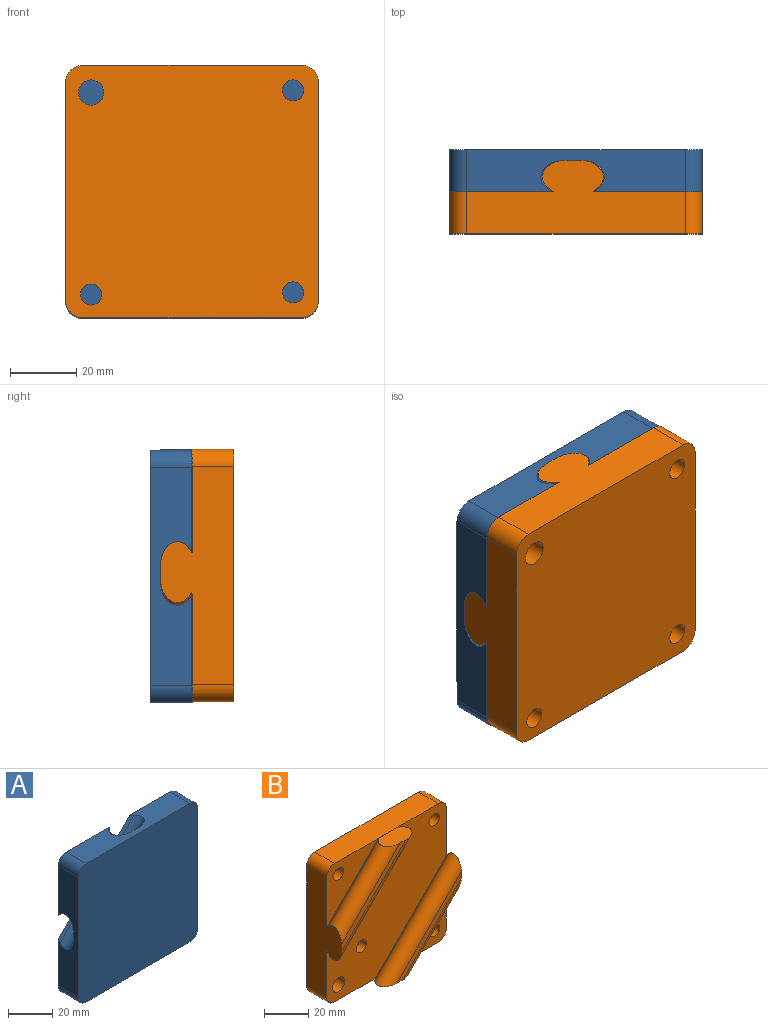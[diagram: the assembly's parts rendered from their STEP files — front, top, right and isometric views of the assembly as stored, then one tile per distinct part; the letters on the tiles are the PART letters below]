
ASSEMBLY  parts=2 mates=1
PART A: 243 faces, bbox 83.4x12.7x83.4 mm
  f0: plane 54.93x54.62mm, normal (0,1,0), area 1341.8mm2, adj f27,f28,f29,f30,f37,f38,f39,f40
  f1: plane 76.2x76.2mm, normal (0,1,0), area 2254mm2, adj f2,f3,f5,f7,f8,f9,f10,f19
  f2: plane 66.04x12.7mm, normal (0,0,-1), area 680.5mm2, adj f1,f4,f5,f14,f15,f18,f20,f22
  f3: plane 66.04x12.7mm, normal (1,0,0), area 680.5mm2, adj f1,f4,f5,f14,f15,f18,f19,f22
  f4: plane 41.48x41.48mm, normal (0,1,0), area 187.6mm2, adj f2,f3,f23,f24
  f5: plane 46.98x46.98mm, normal (0.54,-0.64,-0.54), area 102.9mm2, adj f1,f2,f3,f24
  f6: plane 41.48x41.48mm, normal (0,1,0), area 187.6mm2, adj f7,f8,f25,f26
  f7: plane 66.04x12.7mm, normal (0,0,1), area 680.5mm2, adj f1,f6,f9,f12,f13,f19,f21,f22
  f8: plane 66.04x12.7mm, normal (-1,0,0), area 680.5mm2, adj f1,f6,f9,f12,f13,f20,f21,f22
  f9: plane 46.98x46.98mm, normal (-0.54,-0.64,0.54), area 102.9mm2, adj f1,f7,f8,f26
  f10: cylinder r=3.3mm len=7.59mm, axis (0,1,0), area 157.6mm2, adj f1,f11
  f11: plane 6.6x6.6mm, normal (0,1,0), area 27mm2, adj f10,f16
  f12: plane 32.6x32.6mm, normal (0.54,-0.64,-0.54), area 70.9mm2, adj f7,f8,f13,f25
  f13: plane 32.6x32.6mm, normal (0,1,0), area 525.9mm2, adj f7,f8,f12,f21
  f14: plane 32.6x32.6mm, normal (-0.54,-0.64,0.54), area 70.9mm2, adj f2,f3,f15,f23
  f15: plane 32.6x32.6mm, normal (0,1,0), area 525.9mm2, adj f2,f3,f14,f18
  f16: cylinder r=1.52mm len=3.05mm, axis (0,1,0), area 9.3mm2, adj f11,f17
  f17: plane 3.05x3.05mm, normal (0,1,0), area 7.3mm2, adj f16
  f18: cylinder r=5.08mm len=12.7mm, axis (0,-1,0), area 101.3mm2, adj f2,f3,f15,f22
  f19: cylinder r=5.08mm len=12.7mm, axis (0,1,0), area 101.3mm2, adj f1,f3,f7,f22
  f20: cylinder r=5.08mm len=12.7mm, axis (0,1,0), area 101.3mm2, adj f1,f2,f8,f22
  f21: cylinder r=5.08mm len=12.7mm, axis (0,-1,0), area 101.3mm2, adj f7,f8,f13,f22
  f22: plane 76.2x76.2mm, normal (0,-1,0), area 5784.3mm2, adj f2,f3,f7,f8,f18,f19,f20,f21
  f23: cylinder r=5.08mm len=40.27mm, axis (-0.71,0,-0.71), area 513.1mm2, adj f2,f3,f4,f14
  f24: cylinder r=5.08mm len=52.26mm, axis (0.71,0,0.71), area 760.9mm2, adj f2,f3,f4,f5
  f25: cylinder r=5.08mm len=40.27mm, axis (-0.71,0,-0.71), area 513.1mm2, adj f6,f7,f8,f12
  f26: cylinder r=5.08mm len=52.26mm, axis (-0.71,0,-0.71), area 760.9mm2, adj f6,f7,f8,f9
  f27: plane 21.83x21.27mm, normal (-0.72,0,-0.7), area 271mm2, adj f0,f1,f28,f30
  f28: plane 33.66x32.79mm, normal (-0.7,0,0.72), area 417.7mm2, adj f0,f1,f27,f29
  f29: plane 21.83x21.27mm, normal (0.72,0,0.7), area 271mm2, adj f0,f1,f28,f30
  f30: plane 33.66x32.79mm, normal (0.7,0,-0.72), area 417.7mm2, adj f0,f1,f27,f29
  f31: plane 2.54x0.4mm, normal (-0.7,0,0.71), area 1.4mm2, adj f32,f45,f46,f47
  f32: plane 2.54x1.56mm, normal (-0.71,0,-0.7), area 5.6mm2, adj f31,f33,f46,f47
  f33: plane 2.54x0.5mm, normal (0.7,0,-0.71), area 1.8mm2, adj f32,f34,f46,f47
  f34: extruded ~2.54x0.95mm, area 2.9mm2, adj f33,f35,f46,f47
  f35: extruded ~2.54x0.81mm, area 2.3mm2, adj f34,f36,f46,f47
  f36: extruded ~2.54x0.87mm, area 2.5mm2, adj f35,f45,f46,f47
  f37: extruded ~2.54x1.33mm, area 3.8mm2, adj f0,f38,f44,f46
  f38: extruded ~2.62x2.54mm, area 7.7mm2, adj f0,f37,f39,f46
  f39: plane 2.54x1.04mm, normal (-0.7,0,0.71), area 3.7mm2, adj f0,f38,f40,f46
  f40: plane 3.94x3.91mm, normal (0.71,0,0.7), area 14.1mm2, adj f0,f39,f41,f46
  f41: plane 2.54x0.5mm, normal (0.7,0,-0.71), area 1.8mm2, adj f0,f40,f42,f46
  f42: plane 2.54x1.53mm, normal (-0.71,0,-0.7), area 5.5mm2, adj f0,f41,f43,f46
  f43: plane 2.54x0.45mm, normal (0.7,0,-0.71), area 1.6mm2, adj f0,f42,f44,f46
  f44: extruded ~2.54x1.48mm, area 4.4mm2, adj f0,f37,f43,f46
  f45: extruded ~2.54x1.04mm, area 3.2mm2, adj f31,f36,f46,f47
  f46: plane 6.02x4.43mm, normal (0,1,0), area 8.1mm2, adj f31,f32,f33,f34,f35,f36,f37,f38
  f47: plane 2.67x2.65mm, normal (0,1,0), area 4.1mm2, adj f31,f32,f33,f34,f35,f36,f45
  f48: extruded ~2.54x0.86mm, area 2.5mm2, adj f49,f75,f76,f77
  f49: extruded ~2.54x0.52mm, area 1.5mm2, adj f48,f50,f76,f77
  f50: extruded ~2.54x0.5mm, area 1.4mm2, adj f49,f51,f76,f77
  f51: extruded ~2.54x0.68mm, area 1.9mm2, adj f50,f52,f76,f77
  f52: extruded ~2.54x0.9mm, area 2.7mm2, adj f51,f53,f76,f77
  f53: plane 2.54x0.46mm, normal (0.67,0,-0.74), area 1.6mm2, adj f52,f54,f76,f77
  f54: plane 2.54x0.27mm, normal (0.71,0,0.7), area 1mm2, adj f53,f75,f76,f77
  f55: plane 2.54x0.51mm, normal (0.85,0,0.53), area 1.5mm2, adj f0,f56,f74,f76
  f56: plane 2.54x0.35mm, normal (0.7,0,-0.71), area 1.3mm2, adj f0,f55,f57,f76
  f57: plane 2.54x2.01mm, normal (-0.71,0,-0.7), area 7.2mm2, adj f0,f56,f58,f76
  f58: extruded ~2.54x1.01mm, area 2.9mm2, adj f0,f57,f59,f76
  f59: extruded ~2.54x1.03mm, area 3mm2, adj f0,f58,f60,f76
  f60: extruded ~2.54x0.59mm, area 1.9mm2, adj f0,f59,f61,f76
  f61: extruded ~2.54x0.67mm, area 1.9mm2, adj f0,f60,f62,f76
  f62: plane 2.54x0.51mm, normal (0.92,0,0.38), area 1.4mm2, adj f0,f61,f63,f76
  f63: extruded ~2.54x0.55mm, area 1.5mm2, adj f0,f62,f64,f76
  f64: extruded ~2.54x0.51mm, area 1.6mm2, adj f0,f63,f65,f76
  f65: extruded ~2.54x0.62mm, area 1.8mm2, adj f0,f64,f66,f76
  f66: extruded ~2.54x0.64mm, area 1.9mm2, adj f0,f65,f67,f76
  f67: plane 2.54x0.18mm, normal (0.71,0,0.7), area 0.6mm2, adj f0,f66,f68,f76
  f68: plane 2.54x0.52mm, normal (-0.68,0,0.74), area 1.8mm2, adj f0,f67,f69,f76
  f69: extruded ~2.54x2.35mm, area 6.9mm2, adj f0,f68,f70,f76
  f70: extruded ~2.54x0.89mm, area 2.6mm2, adj f0,f69,f71,f76
  f71: extruded ~2.54x0.91mm, area 2.6mm2, adj f0,f70,f72,f76
  f72: extruded ~2.54x0.65mm, area 2mm2, adj f0,f71,f73,f76
  f73: extruded ~2.54x0.81mm, area 2.1mm2, adj f0,f72,f74,f76
  f74: plane 2.54x0.02mm, normal (0.7,0,-0.71), area 0.1mm2, adj f0,f55,f73,f76
  f75: extruded ~2.54x0.85mm, area 2.5mm2, adj f48,f54,f76,f77
  f76: plane 4.8x4.5mm, normal (0,1,0), area 7.2mm2, adj f48,f49,f50,f51,f52,f53,f54,f55
  f77: plane 2.27x1.72mm, normal (0,1,0), area 2.5mm2, adj f48,f49,f50,f51,f52,f53,f54,f75
  f78: plane 2.54x1.9mm, normal (-0.71,0,-0.7), area 6.8mm2, adj f0,f79,f94,f95
  f79: plane 2.54x0.49mm, normal (-0.7,0,0.71), area 1.8mm2, adj f0,f78,f80,f95
  f80: plane 2.54x1.94mm, normal (0.71,0,0.7), area 6.9mm2, adj f0,f79,f81,f95
  f81: extruded ~2.54x1.09mm, area 3.2mm2, adj f0,f80,f82,f95
  f82: extruded ~2.54x1.05mm, area 3.1mm2, adj f0,f81,f83,f95
  f83: extruded ~2.54x0.68mm, area 2.1mm2, adj f0,f82,f84,f95
  f84: extruded ~2.54x0.7mm, area 1.8mm2, adj f0,f83,f85,f95
  f85: plane 2.54x0.02mm, normal (0.7,0,-0.71), area 0.1mm2, adj f0,f84,f86,f95
  f86: plane 2.54x0.46mm, normal (0.82,0,0.57), area 1.4mm2, adj f0,f85,f87,f95
  f87: plane 2.54x0.4mm, normal (0.7,0,-0.71), area 1.4mm2, adj f0,f86,f88,f95
  f88: plane 2.96x2.93mm, normal (-0.71,0,-0.7), area 10.6mm2, adj f0,f87,f89,f95
  f89: plane 2.54x0.49mm, normal (-0.7,0,0.71), area 1.7mm2, adj f0,f88,f90,f95
  f90: plane 2.54x1.54mm, normal (0.71,0,0.7), area 5.5mm2, adj f0,f89,f91,f95
  f91: extruded ~2.54x1.02mm, area 3.1mm2, adj f0,f90,f92,f95
  f92: extruded ~2.54x0.91mm, area 2.6mm2, adj f0,f91,f93,f95
  f93: extruded ~2.54x0.67mm, area 1.9mm2, adj f0,f92,f94,f95
  f94: extruded ~2.54x0.69mm, area 2mm2, adj f0,f78,f93,f95
  f95: plane 5.44x4.98mm, normal (0,1,0), area 6.8mm2, adj f78,f79,f80,f81,f82,f83,f84,f85
  f96: plane 2.54x0.48mm, normal (0.7,0,-0.71), area 1.7mm2, adj f0,f97,f99,f100
  f97: plane 4.19x4.16mm, normal (-0.71,0,-0.7), area 15mm2, adj f0,f96,f98,f100
  f98: plane 2.54x0.48mm, normal (-0.7,0,0.71), area 1.7mm2, adj f0,f97,f99,f100
  f99: plane 4.19x4.16mm, normal (0.71,0,0.7), area 15mm2, adj f0,f96,f98,f100
  f100: plane 4.67x4.64mm, normal (0,1,0), area 4mm2, adj f96,f97,f98,f99
  f101: plane 3.94x3.91mm, normal (0.71,0,0.7), area 14.1mm2, adj f0,f102,f106,f107
  f102: plane 2.54x2.22mm, normal (0.7,0,-0.71), area 7.9mm2, adj f0,f101,f103,f107
  f103: plane 2.54x0.44mm, normal (-0.71,0,-0.7), area 1.6mm2, adj f0,f102,f104,f107
  f104: plane 2.54x1.72mm, normal (-0.7,0,0.71), area 6.2mm2, adj f0,f103,f105,f107
  f105: plane 3.49x3.47mm, normal (-0.71,0,-0.7), area 12.5mm2, adj f0,f104,f106,f107
  f106: plane 2.54x0.5mm, normal (-0.7,0,0.71), area 1.8mm2, adj f0,f101,f105,f107
  f107: plane 6.13x4.4mm, normal (0,1,0), area 5.4mm2, adj f101,f102,f103,f104,f105,f106
  f108: extruded ~2.54x1.06mm, area 3.2mm2, adj f109,f123,f124,f125
  f109: extruded ~2.54x1.97mm, area 5.8mm2, adj f108,f110,f124,f125
  f110: extruded ~2.54x0.93mm, area 2.6mm2, adj f109,f111,f124,f125
  f111: extruded ~2.54x1.06mm, area 3.2mm2, adj f110,f112,f124,f125
  f112: extruded ~2.54x1.06mm, area 3.2mm2, adj f111,f113,f124,f125
  f113: extruded ~2.54x0.93mm, area 2.6mm2, adj f112,f123,f124,f125
  f114: extruded ~2.54x1.49mm, area 4.4mm2, adj f0,f115,f122,f124
  f115: extruded ~2.54x1.48mm, area 4.3mm2, adj f0,f114,f116,f124
  f116: extruded ~2.54x1.4mm, area 4mm2, adj f0,f115,f117,f124
  f117: extruded ~2.54x1.41mm, area 4mm2, adj f0,f116,f118,f124
  f118: extruded ~2.54x1.48mm, area 4.3mm2, adj f0,f117,f119,f124
  f119: extruded ~2.54x0.98mm, area 3mm2, adj f0,f118,f120,f124
  f120: extruded ~2.54x1.01mm, area 2.6mm2, adj f0,f119,f121,f124
  f121: extruded ~2.54x0.89mm, area 2.7mm2, adj f0,f120,f122,f124
  f122: extruded ~2.54x1.42mm, area 4mm2, adj f0,f114,f121,f124
  f123: extruded ~2.54x0.93mm, area 2.6mm2, adj f108,f113,f124,f125
  f124: plane 4.33x4.28mm, normal (0,1,0), area 7.1mm2, adj f108,f109,f110,f111,f112,f113,f114,f115
  f125: plane 3.21x3.06mm, normal (0,1,0), area 6.4mm2, adj f108,f109,f110,f111,f112,f113,f123
  f126: extruded ~2.54x1.38mm, area 3.9mm2, adj f0,f127,f140,f141
  f127: extruded ~2.54x0.92mm, area 2.8mm2, adj f0,f126,f128,f141
  f128: plane 2.54x0.43mm, normal (-0.71,0,-0.7), area 1.5mm2, adj f0,f127,f129,f141
  f129: extruded ~2.54x0.94mm, area 2.8mm2, adj f0,f128,f130,f141
  f130: extruded ~2.54x0.91mm, area 2.6mm2, adj f0,f129,f131,f141
  f131: extruded ~2.54x1.03mm, area 3.1mm2, adj f0,f130,f132,f141
  f132: extruded ~2.54x1.05mm, area 3.1mm2, adj f0,f131,f133,f141
  f133: extruded ~2.54x0.94mm, area 2.7mm2, adj f0,f132,f134,f141
  f134: extruded ~2.54x0.77mm, area 2.3mm2, adj f0,f133,f135,f141
  f135: plane 2.54x0.55mm, normal (-0.42,0,-0.91), area 1.5mm2, adj f0,f134,f136,f141
  f136: extruded ~2.54x0.46mm, area 1.3mm2, adj f0,f135,f137,f141
  f137: extruded ~2.54x0.47mm, area 1.5mm2, adj f0,f136,f138,f141
  f138: extruded ~2.54x1.42mm, area 4.1mm2, adj f0,f137,f139,f141
  f139: extruded ~2.54x1.5mm, area 4.4mm2, adj f0,f138,f140,f141
  f140: extruded ~2.54x1.48mm, area 4.3mm2, adj f0,f126,f139,f141
  f141: plane 4.33x4.28mm, normal (0,1,0), area 4.9mm2, adj f126,f127,f128,f129,f130,f131,f132,f133
  f142: plane 2.54x0.37mm, normal (0.12,0,0.99), area 1mm2, adj f0,f143,f157,f158
  f143: plane 2.54x0.02mm, normal (-0.7,0,0.71), area 0.1mm2, adj f0,f142,f144,f158
  f144: plane 2.54x0.5mm, normal (-0.68,0,-0.74), area 1.7mm2, adj f0,f143,f145,f158
  f145: plane 2.54x2.19mm, normal (-0.71,0,-0.7), area 7.8mm2, adj f0,f144,f146,f158
  f146: plane 2.54x0.48mm, normal (-0.7,0,0.71), area 1.7mm2, adj f0,f145,f147,f158
  f147: plane 4.19x4.16mm, normal (0.71,0,0.7), area 15mm2, adj f0,f146,f148,f158
  f148: plane 2.54x0.48mm, normal (0.7,0,-0.71), area 1.7mm2, adj f0,f147,f149,f158
  f149: plane 2.54x1.08mm, normal (-0.71,0,-0.7), area 3.9mm2, adj f0,f148,f150,f158
  f150: plane 2.54x0.63mm, normal (0.06,0,-1), area 1.6mm2, adj f0,f149,f151,f158
  f151: plane 2.54x2.4mm, normal (0.99,0,0.14), area 6.1mm2, adj f0,f150,f152,f158
  f152: plane 2.54x0.58mm, normal (0.7,0,-0.71), area 2.1mm2, adj f0,f151,f153,f158
  f153: plane 2.96x2.54mm, normal (-0.99,0,-0.13), area 7.6mm2, adj f0,f152,f154,f158
  f154: plane 2.54x2.45mm, normal (-0.03,0,-1), area 6.2mm2, adj f0,f153,f155,f158
  f155: plane 2.54x0.57mm, normal (-0.7,0,0.71), area 2mm2, adj f0,f154,f156,f158
  f156: plane 2.54x1.94mm, normal (0.03,0,1), area 4.9mm2, adj f0,f155,f157,f158
  f157: plane 2.54x0.41mm, normal (0.1,0,1), area 1.1mm2, adj f0,f142,f156,f158
  f158: plane 6.59x5.28mm, normal (0,1,0), area 7.5mm2, adj f142,f143,f144,f145,f146,f147,f148,f149
  f159: plane 2.54x1.89mm, normal (0.71,0,0.7), area 6.8mm2, adj f0,f160,f176,f177
  f160: plane 2.54x0.48mm, normal (0.7,0,-0.71), area 1.7mm2, adj f0,f159,f161,f177
  f161: plane 2.54x1.92mm, normal (-0.71,0,-0.7), area 6.9mm2, adj f0,f160,f162,f177
  f162: extruded ~2.54x1.09mm, area 3.2mm2, adj f0,f161,f163,f177
  f163: extruded ~2.54x1.06mm, area 3.1mm2, adj f0,f162,f164,f177
  f164: extruded ~2.54x0.67mm, area 2mm2, adj f0,f163,f165,f177
  f165: extruded ~2.54x0.71mm, area 1.8mm2, adj f0,f164,f166,f177
  f166: plane 2.54x0.03mm, normal (-0.7,0,0.71), area 0.1mm2, adj f0,f165,f167,f177
  f167: extruded ~2.54x0.44mm, area 1.5mm2, adj f0,f166,f168,f177
  f168: plane 2.54x1.23mm, normal (-0.71,0,-0.7), area 4.4mm2, adj f0,f167,f169,f177
  f169: plane 2.54x0.48mm, normal (-0.7,0,0.71), area 1.7mm2, adj f0,f168,f170,f177
  f170: plane 4.19x4.16mm, normal (0.71,0,0.7), area 15mm2, adj f0,f169,f171,f177
  f171: plane 2.54x0.48mm, normal (0.7,0,-0.71), area 1.7mm2, adj f0,f170,f172,f177
  f172: plane 2.54x1.53mm, normal (-0.71,0,-0.7), area 5.5mm2, adj f0,f171,f173,f177
  f173: extruded ~2.54x1.03mm, area 3.1mm2, adj f0,f172,f174,f177
  f174: extruded ~2.54x0.91mm, area 2.6mm2, adj f0,f173,f175,f177
  f175: extruded ~2.54x0.67mm, area 2mm2, adj f0,f174,f176,f177
  f176: extruded ~2.54x0.7mm, area 2.1mm2, adj f0,f159,f175,f177
  f177: plane 6.66x4.96mm, normal (0,1,0), area 7.9mm2, adj f159,f160,f161,f162,f163,f164,f165,f166
  f178: extruded ~2.54x0.86mm, area 2.5mm2, adj f179,f205,f206,f207
  f179: extruded ~2.54x0.52mm, area 1.5mm2, adj f178,f180,f206,f207
  f180: extruded ~2.54x0.5mm, area 1.4mm2, adj f179,f181,f206,f207
  f181: extruded ~2.54x0.68mm, area 1.9mm2, adj f180,f182,f206,f207
  f182: extruded ~2.54x0.9mm, area 2.7mm2, adj f181,f183,f206,f207
  f183: plane 2.54x0.46mm, normal (0.67,0,-0.74), area 1.6mm2, adj f182,f184,f206,f207
  f184: plane 2.54x0.27mm, normal (0.71,0,0.7), area 1mm2, adj f183,f205,f206,f207
  f185: plane 2.54x0.51mm, normal (0.85,0,0.53), area 1.5mm2, adj f0,f186,f204,f206
  f186: plane 2.54x0.35mm, normal (0.7,0,-0.71), area 1.3mm2, adj f0,f185,f187,f206
  f187: plane 2.54x2.01mm, normal (-0.71,0,-0.7), area 7.2mm2, adj f0,f186,f188,f206
  f188: extruded ~2.54x1.01mm, area 2.9mm2, adj f0,f187,f189,f206
  f189: extruded ~2.54x1.03mm, area 3mm2, adj f0,f188,f190,f206
  f190: extruded ~2.54x0.59mm, area 1.9mm2, adj f0,f189,f191,f206
  f191: extruded ~2.54x0.67mm, area 1.9mm2, adj f0,f190,f192,f206
  f192: plane 2.54x0.51mm, normal (0.92,0,0.38), area 1.4mm2, adj f0,f191,f193,f206
  f193: extruded ~2.54x0.55mm, area 1.5mm2, adj f0,f192,f194,f206
  f194: extruded ~2.54x0.51mm, area 1.6mm2, adj f0,f193,f195,f206
  f195: extruded ~2.54x0.62mm, area 1.8mm2, adj f0,f194,f196,f206
  f196: extruded ~2.54x0.64mm, area 1.9mm2, adj f0,f195,f197,f206
  f197: plane 2.54x0.18mm, normal (0.71,0,0.7), area 0.6mm2, adj f0,f196,f198,f206
  f198: plane 2.54x0.52mm, normal (-0.68,0,0.74), area 1.8mm2, adj f0,f197,f199,f206
  f199: extruded ~2.54x2.35mm, area 6.9mm2, adj f0,f198,f200,f206
  f200: extruded ~2.54x0.89mm, area 2.6mm2, adj f0,f199,f201,f206
  f201: extruded ~2.54x0.91mm, area 2.6mm2, adj f0,f200,f202,f206
  f202: extruded ~2.54x0.65mm, area 2mm2, adj f0,f201,f203,f206
  f203: extruded ~2.54x0.81mm, area 2.1mm2, adj f0,f202,f204,f206
  f204: plane 2.54x0.02mm, normal (0.7,0,-0.71), area 0.1mm2, adj f0,f185,f203,f206
  f205: extruded ~2.54x0.85mm, area 2.5mm2, adj f178,f184,f206,f207
  f206: plane 4.8x4.5mm, normal (0,1,0), area 7.2mm2, adj f178,f179,f180,f181,f182,f183,f184,f185
  f207: plane 2.27x1.72mm, normal (0,1,0), area 2.5mm2, adj f178,f179,f180,f181,f182,f183,f184,f205
  f208: extruded ~2.54x0.38mm, area 1.3mm2, adj f0,f209,f221,f222
  f209: extruded ~2.54x0.65mm, area 1.9mm2, adj f0,f208,f210,f222
  f210: extruded ~2.54x0.84mm, area 2.2mm2, adj f0,f209,f211,f222
  f211: plane 2.54x0.02mm, normal (-0.7,0,0.71), area 0.1mm2, adj f0,f210,f212,f222
  f212: plane 2.54x0.59mm, normal (-0.78,0,-0.63), area 1.9mm2, adj f0,f211,f213,f222
  f213: plane 2.54x0.4mm, normal (-0.7,0,0.71), area 1.4mm2, adj f0,f212,f214,f222
  f214: plane 2.96x2.93mm, normal (0.71,0,0.7), area 10.6mm2, adj f0,f213,f215,f222
  f215: plane 2.54x0.48mm, normal (0.7,0,-0.71), area 1.7mm2, adj f0,f214,f216,f222
  f216: plane 2.54x1.58mm, normal (-0.71,0,-0.7), area 5.6mm2, adj f0,f215,f217,f222
  f217: extruded ~2.54x0.61mm, area 1.9mm2, adj f0,f216,f218,f222
  f218: extruded ~2.54x0.67mm, area 1.7mm2, adj f0,f217,f219,f222
  f219: extruded ~2.54x0.56mm, area 1.6mm2, adj f0,f218,f220,f222
  f220: extruded ~2.54x0.36mm, area 1.2mm2, adj f0,f219,f221,f222
  f221: plane 2.54x0.5mm, normal (-0.61,0,-0.79), area 1.6mm2, adj f0,f208,f220,f222
  f222: plane 4.68x3.44mm, normal (0,1,0), area 3.9mm2, adj f208,f209,f210,f211,f212,f213,f214,f215
  f223: extruded ~2.54x0.24mm, area 0.8mm2, adj f0,f224,f241,f242
  f224: extruded ~2.54x0.48mm, area 1.4mm2, adj f0,f223,f225,f242
  f225: extruded ~2.54x0.52mm, area 1.5mm2, adj f0,f224,f226,f242
  f226: plane 2.54x1.71mm, normal (-0.71,0,-0.7), area 6.1mm2, adj f0,f225,f227,f242
  f227: plane 2.54x0.85mm, normal (0.7,0,-0.71), area 3.1mm2, adj f0,f226,f228,f242
  f228: plane 2.54x0.38mm, normal (-0.71,0,-0.7), area 1.3mm2, adj f0,f227,f229,f242
  f229: plane 2.54x0.85mm, normal (-0.7,0,0.71), area 3.1mm2, adj f0,f228,f230,f242
  f230: plane 2.54x0.68mm, normal (-0.71,0,-0.7), area 2.4mm2, adj f0,f229,f231,f242
  f231: plane 2.54x0.29mm, normal (-0.7,0,0.71), area 1mm2, adj f0,f230,f232,f242
  f232: plane 2.54x0.82mm, normal (0.47,0,0.88), area 2.4mm2, adj f0,f231,f233,f242
  f233: plane 2.54x0.62mm, normal (-0.34,0,0.94), area 1.7mm2, adj f0,f232,f234,f242
  f234: plane 2.54x0.23mm, normal (0.71,0,0.7), area 0.8mm2, adj f0,f233,f235,f242
  f235: plane 2.54x0.42mm, normal (0.7,0,-0.71), area 1.5mm2, adj f0,f234,f236,f242
  f236: plane 2.54x1.72mm, normal (0.71,0,0.7), area 6.2mm2, adj f0,f235,f237,f242
  f237: extruded ~2.54x1.77mm, area 5.2mm2, adj f0,f236,f238,f242
  f238: extruded ~2.54x0.32mm, area 1mm2, adj f0,f237,f239,f242
  f239: extruded ~2.54x0.27mm, area 0.8mm2, adj f0,f238,f240,f242
  f240: plane 2.54x0.37mm, normal (-0.71,0,-0.7), area 1.3mm2, adj f0,f239,f241,f242
  f241: extruded ~2.54x0.23mm, area 0.7mm2, adj f0,f223,f240,f242
  f242: plane 4.76x4.05mm, normal (0,1,0), area 4.8mm2, adj f223,f224,f225,f226,f227,f228,f229,f230
PART B: 32 faces, bbox 83.4x22.2x83.4 mm
  f0: cylinder r=3.25mm len=6.5mm, axis (0,-1,0), area 90.8mm2, adj f7,f25
  f1: plane 76.2x76.19mm, normal (0,1,0), area 5642.8mm2, adj f2,f4,f12,f15,f17,f18,f19,f20
  f2: plane 66.03x22.2mm, normal (1,0,0), area 988.6mm2, adj f1,f3,f5,f6,f7,f16,f17,f19
  f3: plane 32.93x32.93mm, normal (0.54,0.64,-0.54), area 68.7mm2, adj f2,f4,f16,f21
  f4: plane 66.04x22.2mm, normal (0,0,-1), area 988.9mm2, adj f1,f3,f5,f6,f7,f16,f17,f18
  f5: plane 46.6x46.58mm, normal (-0.54,0.64,0.54), area 97.8mm2, adj f2,f4,f7,f22
  f6: plane 41.09x41.08mm, normal (0,-1,0), area 157.3mm2, adj f2,f4,f21,f22
  f7: plane 76.2x76.19mm, normal (0,-1,0), area 3639.6mm2, adj f0,f2,f4,f5,f11,f12,f15,f18
  f8: plane 12.43x0.01mm, normal (0,1,0), area 0.1mm2, adj f9,f10,f11,f15
  f9: plane 32.93x32.92mm, normal (-0.54,0.64,0.54), area 68.7mm2, adj f8,f10,f12,f14,f15,f24
  f10: plane 18.4x9.45mm, normal (0,0,1), area 149.6mm2, adj f8,f9,f11,f13,f23,f24
  f11: plane 46.6x46.58mm, normal (0.54,0.64,-0.54), area 97.8mm2, adj f7,f8,f10,f12,f15,f23
  f12: plane 66.03x22.2mm, normal (-1,0,0), area 988.6mm2, adj f1,f7,f9,f11,f13,f14,f18,f20
  f13: plane 41.09x41.08mm, normal (0,-1,0), area 157.3mm2, adj f10,f12,f23,f24
  f14: plane 32.92x32.92mm, normal (0,-1,0), area 504.5mm2, adj f9,f12,f15,f20,f29
  f15: plane 66.04x12.75mm, normal (0,0,1), area 839.3mm2, adj f1,f7,f8,f9,f11,f14,f19,f20
  f16: plane 32.93x32.93mm, normal (0,-1,0), area 504.9mm2, adj f2,f3,f4,f17,f28
  f17: cylinder r=5.08mm len=12.7mm, axis (0,1,0), area 101.3mm2, adj f1,f2,f4,f16
  f18: cylinder r=5.08mm len=12.7mm, axis (0,-1,0), area 101.3mm2, adj f1,f4,f7,f12
  f19: cylinder r=5.08mm len=12.7mm, axis (0,1,0), area 101.3mm2, adj f1,f2,f7,f15
  f20: cylinder r=5.08mm len=12.7mm, axis (0,-1,0), area 101.3mm2, adj f1,f12,f14,f15
  f21: cylinder r=5.08mm len=40.65mm, axis (-0.71,0,-0.71), area 519.3mm2, adj f2,f3,f4,f6
  f22: cylinder r=5.08mm len=51.88mm, axis (-0.71,0,-0.71), area 754.5mm2, adj f2,f4,f5,f6
  f23: cylinder r=5.08mm len=51.88mm, axis (-0.71,0,-0.71), area 754.5mm2, adj f10,f11,f12,f13
  f24: cylinder r=5.08mm len=40.65mm, axis (-0.71,0,-0.71), area 519.3mm2, adj f9,f10,f12,f13
  f25: plane 6.5x6.5mm, normal (0,-1,0), area 26.1mm2, adj f0,f26
  f26: cylinder r=1.5mm len=3mm, axis (0,-1,0), area 9.4mm2, adj f25,f27
  f27: plane 3x3mm, normal (0,-1,0), area 7.1mm2, adj f26
  f28: cylinder r=3.17mm len=12.7mm, axis (0,1,0), area 253.4mm2, adj f1,f16
  f29: cylinder r=3.17mm len=12.7mm, axis (0,1,0), area 253.4mm2, adj f1,f14
  f30: cylinder r=3.81mm len=12.7mm, axis (0,1,0), area 304mm2, adj f1,f7
  f31: cylinder r=3.17mm len=12.7mm, axis (0,1,0), area 253.4mm2, adj f1,f7
PLACE A rot(axis=(0,0,1),180deg) t=(-47.89,-13.13,-3.73)mm
PLACE B rot(axis=(-1,0,0),180deg) t=(2.96,-13,47.42)mm fixed
MATE slider A.f24 <-> B.f23  axis (-0.71,0,0.71) through (-64.48,-8.63,28.93)mm
